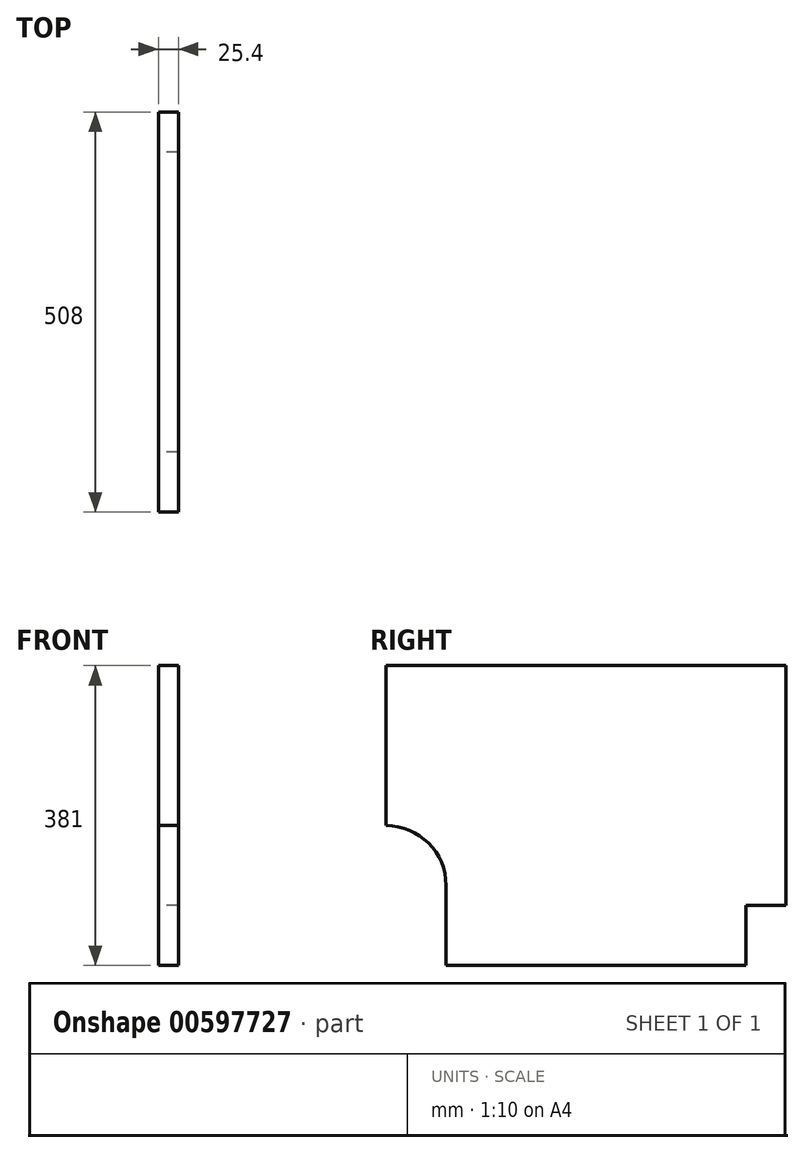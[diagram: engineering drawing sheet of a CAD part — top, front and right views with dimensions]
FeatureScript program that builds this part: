
annotation { "Feature Type Name" : "Feature", "Feature Type Description" : "" }
export const myFeature = defineFeature(function(context is Context, id is Id, definition is map)
    precondition{}
    {
        {
            var Q0;
            Q0=qCreatedBy(makeId("Right.planeOp"),FACE);
            var sketch = newSketch(context, id + "F0", { "sketchPlane" : qUnion([Q0])});
            skLineSegment(sketch, "E0", {"start": v(-457.2, 381) * mm, "end": v(50.8, 381) * mm});
            skLineSegment(sketch, "E1", {"start": v(50.8, 381) * mm, "end": v(50.8, 76.2) * mm});
            skLineSegment(sketch, "E2", {"start": v(50.8, 76.2) * mm, "end": v(0, 76.2) * mm});
            skLineSegment(sketch, "E3", {"start": v(0, 76.2) * mm, "end": v(0, 0) * mm});
            skLineSegment(sketch, "E4", {"start": v(0, 0) * mm, "end": v(-381, 0) * mm});
            skLineSegment(sketch, "E5", {"start": v(-381, 0) * mm, "end": v(-381, 101.6) * mm});
            skLineSegment(sketch, "E6", {"start": v(-457.2, 177.8) * mm, "end": v(-457.2, 177.8) * mm});
            skLineSegment(sketch, "E7", {"start": v(-457.2, 177.8) * mm, "end": v(-457.2, 381) * mm});
            skPoint(sketch, "E8.visualSharp", {"position": v(-381, 177.8) * mm});
            skArc(sketch, "E8.filletArc", {"start": v(-381, 101.6) * mm, "mid": v(-403.32, 155.48) * mm, "end": v(-457.2, 177.8) * mm});
            skSolve(sketch);
        }
        {
            var Q0;
            Q0 = qSketchRegion(id + "F0", true);
            extrude(context, id + "F1", {"entities" : qUnion([Q0]), "depth" : 25.4 * mm, "offsetDistance" : 25.4 * mm});
        }
    });
